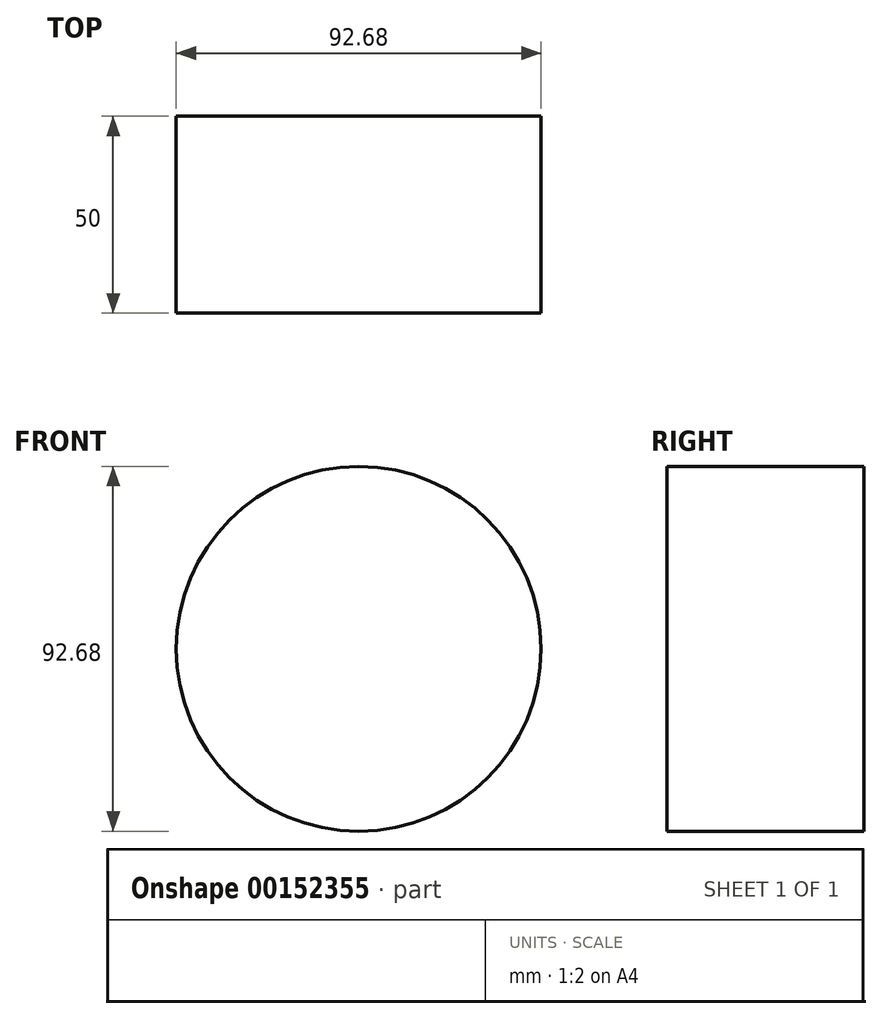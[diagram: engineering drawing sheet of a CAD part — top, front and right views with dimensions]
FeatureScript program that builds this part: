
annotation { "Feature Type Name" : "Feature", "Feature Type Description" : "" }
export const myFeature = defineFeature(function(context is Context, id is Id, definition is map)
    precondition{}
    {
        {
            var Q0;
            Q0=qCreatedBy(makeId("Front.planeOp"), FACE);
            var sketch = newSketch(context, id + "F0", { "sketchPlane" : qUnion([Q0])});
            skCircle(sketch, "E0", {"center": v(0, 0) * mm, "radius": 46.34 * mm});
            skSolve(sketch);
        }
        {
            var Q0;
            Q0 = qSketchRegion(id + "F0", true);
            extrude(context, id + "F1", {"entities" : qUnion([Q0]), "domain" : OperationDomain.MODEL, "flatOperationType" : FlatOperationType.REMOVE, "depth" : 50 * mm, "offsetDistance" : 25 * mm, "symmetric" : true});
        }
    });
